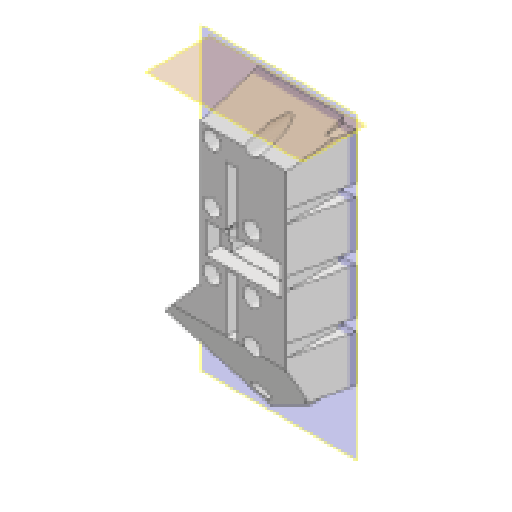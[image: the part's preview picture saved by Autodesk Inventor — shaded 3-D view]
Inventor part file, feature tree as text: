
AUTODESK INVENTOR PART (.ipt)
format: ipt  version: 2025.1 (Build 291241020, 241B)  size: 394,752 bytes
history: native  units: in
note: dims shown in document units (in); Inventor stores cm internally (conversion verified against a paired STEP export)
features: reference x48, extrude x13, sketch x13, other x12, plane x2, chamfer x1, projected_geometry x1
ambient origin geometry x8: Origin, YZ Plane, XZ Plane, XY Plane, X Axis, Y Axis, Z Axis, Center Point
bodies: Solid1 (feature_tree)
feature tree (90):
  extrude  "Extrusion1"  Depth=0.25in TaperAngle=0.0deg
  extrude  "Extrusion2"  Depth=0.14in
  extrude  "Extrusion3"  Depth=0.14in
  plane  "Work Plane1"
  extrude  "Extrusion4"  Depth=0.14in
  extrude  "Extrusion5"  Depth=0.35in TaperAngle=0.0deg
  extrude  "Extrusion6"  Depth=0.3in
  plane  "Work Plane2"
  extrude  "Extrusion7"  Depth=0.3in
  extrude  "Extrusion9"  Depth=0.3in TaperAngle=0.0deg
  extrude  "Extrusion10"  Depth=0.7in
  extrude  "Extrusion11"  Depth=0.3in
  extrude  "Extrusion12"  Depth=0.25in
  extrude  "Extrusion13"  Depth=0.3in
  extrude  "Extrusion14"  Depth=0.3in
  chamfer  "Chamfer1"  Distance=0.75in
  sketch  "Sketch1"  dims[d0=0.25in d1=0.0in d2=0.25in d3=0.0in]
  reference  "Reference1"
  reference  "Reference2"
  reference  "Reference3"
  reference  "Reference4"
  reference  "Reference5"
  reference  "Reference6"
  reference  "Reference7"
  reference  "Reference8"
  reference  "Reference9"
  reference  "Reference10"
  reference  "Reference11"
  reference  "Reference12"
  reference  "Reference13"
  reference  "Reference14"
  reference  "Reference15"
  reference  "Reference16"
  reference  "Reference17"
  reference  "Reference18"
  reference  "Reference19"
  reference  "Reference20"
  reference  "Reference21"
  reference  "Reference22"
  reference  "Reference23"
  reference  "Reference24"
  reference  "Reference25"
  reference  "Reference26"
  reference  "Reference27"
  sketch  "Sketch2"  dims[d4=0.7in d5=0.14in d7=0.14in]
  reference  "Reference28"
  reference  "Reference29"
  reference  "Reference30"
  reference  "Reference31"
  reference  "Reference32"
  reference  "Reference33"
  reference  "Reference34"
  reference  "Reference35"
  reference  "Reference36"
  reference  "Reference37"
  reference  "Reference38"
  reference  "Reference39"
  reference  "Reference40"
  reference  "Reference41"
  reference  "Reference42"
  reference  "Reference43"
  sketch  "Sketch3"  dims[d8=0.14in d9=0.14in]
  reference  "Reference44"
  reference  "Reference45"
  reference  "Reference46"
  sketch  "Sketch5"  dims[d10=0.14in d12=0.14in]
  sketch  "Sketch6"  dims[d13=0.35in d14=0.25in d15=0.0in]
  sketch  "Sketch7"  dims[d16=-0.1in d17=0.3in]
  projected_geometry  "Projected Loop1"
  sketch  "Sketch8"  dims[d19=0.3in d20=0.3in]
  sketch  "Sketch10"  dims[d22=0.3in d25=0.25in d26=0.0in]
  reference  "Reference48"
  sketch  "Sketch11"  dims[d27=0.14in d28=0.7in]
  sketch  "Sketch12"  dims[d29=0.25in d30=0.3in]
  sketch  "Sketch13"  dims[d31=0.14in d32=0.25in]
  sketch  "Sketch14"  dims[d33=0.3in d34=0.14in]
  sketch  "Sketch15"  dims[d35=0.3in d36=0.3in d37=0.75in d38=0.0in d40=4.25in d41=0.0in d42=0.25in d43=1.4in d44=0.325in d45=6.3125in d46=0.0in d52=0.6in d53=0.0in d54=0.5in d55=0.9in d56=0.3in d57=0.25in d58=0.873in d59=0.0in d60=0.2in d61=0.055in d62=0.928in d63=0.0in d64=1.1in d65=0.07in d66=0.07in d67=0.55in d68=0.655in d69=0.0in d70=0.52in d71=1.3in d72=0.65in d73=0.255in d74=0.0in d75=2.625in d76=0.0in d77=0.1in d78=0.125in d79=45.0deg]
  reference  "Reference49"
  parser-record x1  (decoder bookkeeping rows leaked as tree rows — omitted from the tree; the rows remain in map.json)
  other  "Hand Assem.iam"
  other  "Thumb Base2:1"
  other  "PALM 3:1"
  other  "PALM 2:1"
  other  "PALM 1:1"
  other  "KNUCKLE 1:1"
  other  "KNUCKLE 2:1"
  other  "KNUCKLE 3:1"
  other  "PALM 4:1"
  other  "KNUCKLE 4:1"
  other  "Palm:1"
note: 1 file-system path scrubbed to <path> (originals preserved in map.json)
